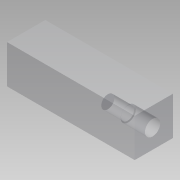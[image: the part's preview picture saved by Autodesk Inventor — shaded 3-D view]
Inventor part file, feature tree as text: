
AUTODESK INVENTOR PART (.ipt)
format: ipt  version: 2014 (Build 180170000, 170)  size: 129,536 bytes
history: native  units: mm
features: other x48, extrude x4, sketch x4
ambient origin geometry x8: Origin, YZ Plane, XZ Plane, XY Plane, X Axis, Y Axis, Z Axis, Center Point
bodies: 实体1 (feature_tree)
feature tree (56):
  extrude  "拉伸1"  Depth=35.05mm
  other  "UCS1"
  other  "UCS2"
  other  "UCS3"
  other  "UCS4"
  other  "UCS5"
  other  "UCS6"
  extrude  "拉伸2"  Depth=35.05mm
  extrude  "拉伸3"  Depth=35.05mm
  extrude  "拉伸4"  Depth=35.05mm TaperAngle=0.0deg
  sketch  "草图1"  dims[d0=30.0mm d1=0.0mm]
  sketch  "草图2"  dims[d2=0.0mm d3=0.0mm d4=0.0mm d5=0.0mm d6=0.0mm d7=0.0mm]
  sketch  "草图3"  dims[d8=0.0mm d9=0.0mm d10=0.0mm d11=0.0mm d12=0.0mm d13=0.0mm]
  sketch  "草图4"  dims[d14=0.0mm d15=0.0mm d16=0.0mm d17=0.0mm d18=0.0mm d19=0.0mm d20=0.0mm d21=0.0mm d22=0.0mm d23=0.0mm d24=0.0mm d25=0.0mm d26=0.0mm d27=0.0mm d28=0.0mm d29=0.0mm d30=0.0mm d31=0.0mm d32=0.0mm d33=0.0mm d34=0.0mm d35=0.0mm d36=0.0mm d37=0.0mm d38=12.0mm d39=14.0mm d40=15.0mm d41=19.05mm d42=0.0mm d43=19.05mm d44=-10.471976mm d45=10.25mm d46=35.05mm d47=0.0mm]
  other  "UCS1: YZ 平面"
  other  "UCS1: XZ 平面"
  other  "UCS1: XY 平面"
  other  "UCS1: X 轴"
  other  "UCS1: Y 轴"
  other  "UCS1: Z 轴"
  other  "UCS1: 原点"
  other  "UCS2: YZ 平面"
  other  "UCS2: XZ 平面"
  other  "UCS2: XY 平面"
  other  "UCS2: X 轴"
  other  "UCS2: Y 轴"
  other  "UCS2: Z 轴"
  other  "UCS2: 原点"
  other  "UCS3: YZ 平面"
  other  "UCS3: XZ 平面"
  other  "UCS3: XY 平面"
  other  "UCS3: X 轴"
  other  "UCS3: Y 轴"
  other  "UCS3: Z 轴"
  other  "UCS3: 原点"
  other  "UCS4: YZ 平面"
  other  "UCS4: XZ 平面"
  other  "UCS4: XY 平面"
  other  "UCS4: X 轴"
  other  "UCS4: Y 轴"
  other  "UCS4: Z 轴"
  other  "UCS4: 原点"
  other  "UCS5: YZ 平面"
  other  "UCS5: XZ 平面"
  other  "UCS5: XY 平面"
  other  "UCS5: X 轴"
  other  "UCS5: Y 轴"
  other  "UCS5: Z 轴"
  other  "UCS5: 原点"
  other  "UCS6: YZ 平面"
  other  "UCS6: XZ 平面"
  other  "UCS6: XY 平面"
  other  "UCS6: X 轴"
  other  "UCS6: Y 轴"
  other  "UCS6: Z 轴"
  other  "UCS6: 原点"
